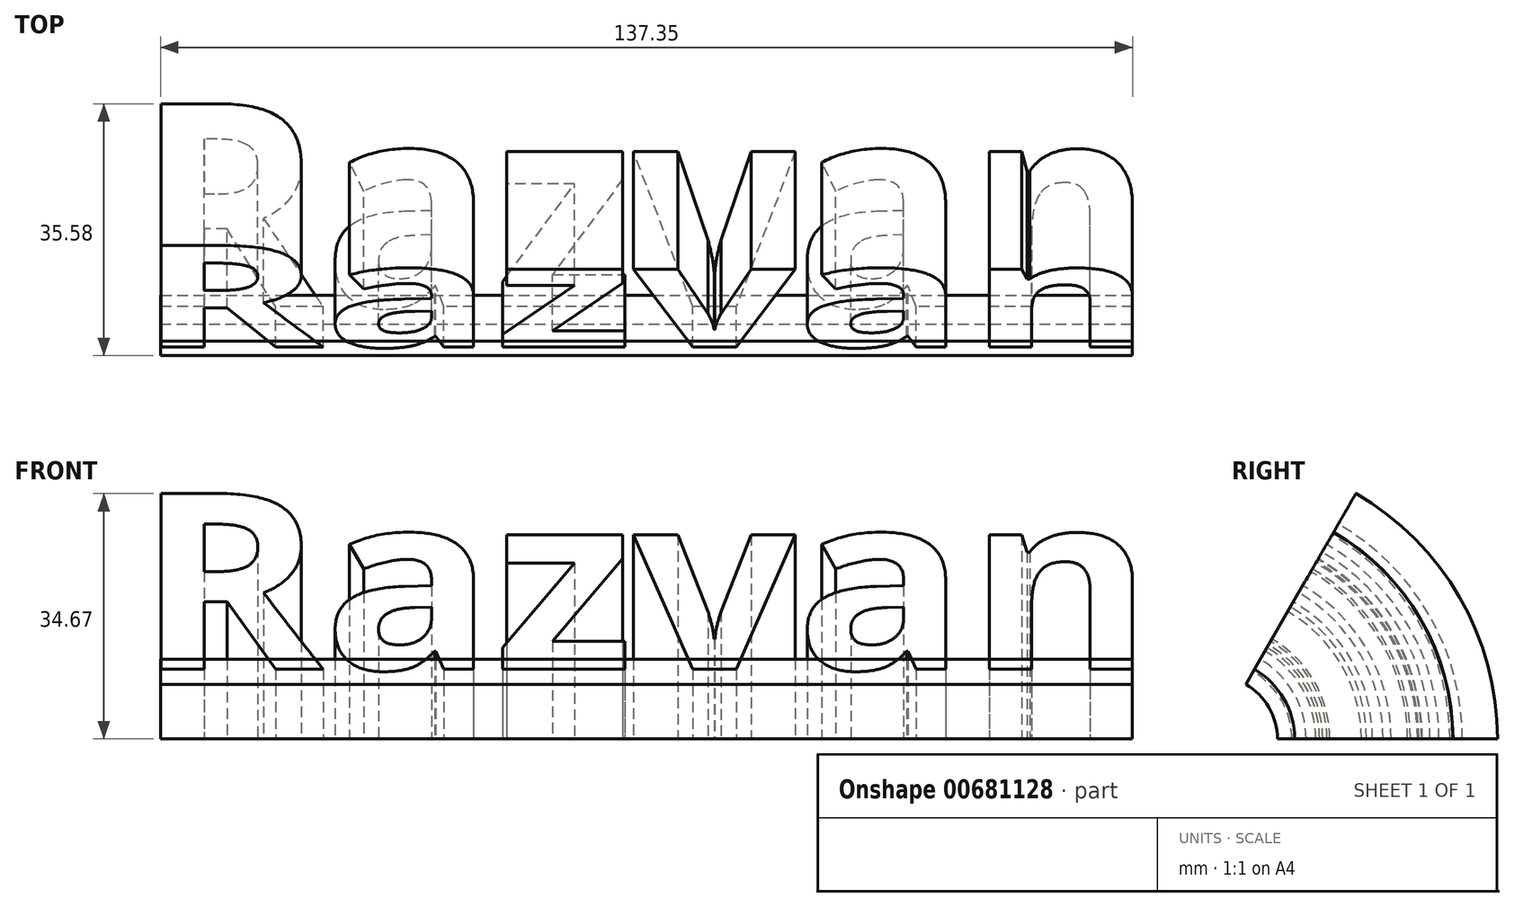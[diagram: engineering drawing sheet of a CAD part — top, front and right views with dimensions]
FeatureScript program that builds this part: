
annotation { "Feature Type Name" : "Feature", "Feature Type Description" : "" }
export const myFeature = defineFeature(function(context is Context, id is Id, definition is map)
    precondition{}
    {
        {
            var Q0;
            Q0=qCreatedBy(makeId("Top.planeOp"),FACE);
            var sketch = newSketch(context, id + "F0", { "sketchPlane" : qUnion([Q0])});
            skText(sketch, "E0", { "text": "Razvan", "fontName": "OpenSans-Bold.ttf"});
            const initialGuessF0  = {"E0": [-0.07616, -0.01101, 1, 0, 0.02892]};
            skSetInitialGuess(sketch, initialGuessF0);
            skSolve(sketch);
        }
        {
            var Q0;
            Q0=qCreatedBy(makeId("Top.planeOp"),FACE);
            var sketch = newSketch(context, id + "F1", { "sketchPlane" : qUnion([Q0])});
            skLineSegment(sketch, "E1.bottom", {"start": v(-72.64, -9.4) * mm, "end": v(64.67, -9.4) * mm});
            skLineSegment(sketch, "E1.top", {"start": v(-72.64, -13.45) * mm, "end": v(64.67, -13.45) * mm});
            skLineSegment(sketch, "E1.left", {"start": v(-72.64, -9.4) * mm, "end": v(-72.64, -13.45) * mm});
            skLineSegment(sketch, "E1.right", {"start": v(64.67, -9.4) * mm, "end": v(64.67, -13.45) * mm});
            skSolve(sketch);
        }
        {
            var Q0;
            Q0=qCreatedBy(makeId("Top.planeOp"),FACE);
            var sketch = newSketch(context, id + "F2", { "sketchPlane" : qUnion([Q0])});
            skLineSegment(sketch, "E2", {"start": v(-82.92, -22.37) * mm, "end": v(83.6, -22.37) * mm});
            skSolve(sketch);
        }
        {
            var Q0;
            Q0 = qSketchRegion(id + "F0", true);
            var Q1;
            Q1=makeQuery(id+"F1.imprint","IMPRINT",FACE,{"disambiguationData":[TD([[makeQuery(id+"F1.imprint","IMPRINT",EDGE,{"derivedFrom":sQuery(id+"F1.wireOp",EDGE,"E1.bottom")}),-1.0]])]});
            var Q2;
            Q2=sQuery(id+"F2.wireOp",EDGE,"E2");
            revolve(context, id + "F3", {"entities" : qUnion([Q0, Q1]), "axis" : qUnion([Q2]), "revolveType" : RevolveType.ONE_DIRECTION, "angle" : 60 * degree});
        }
    });
